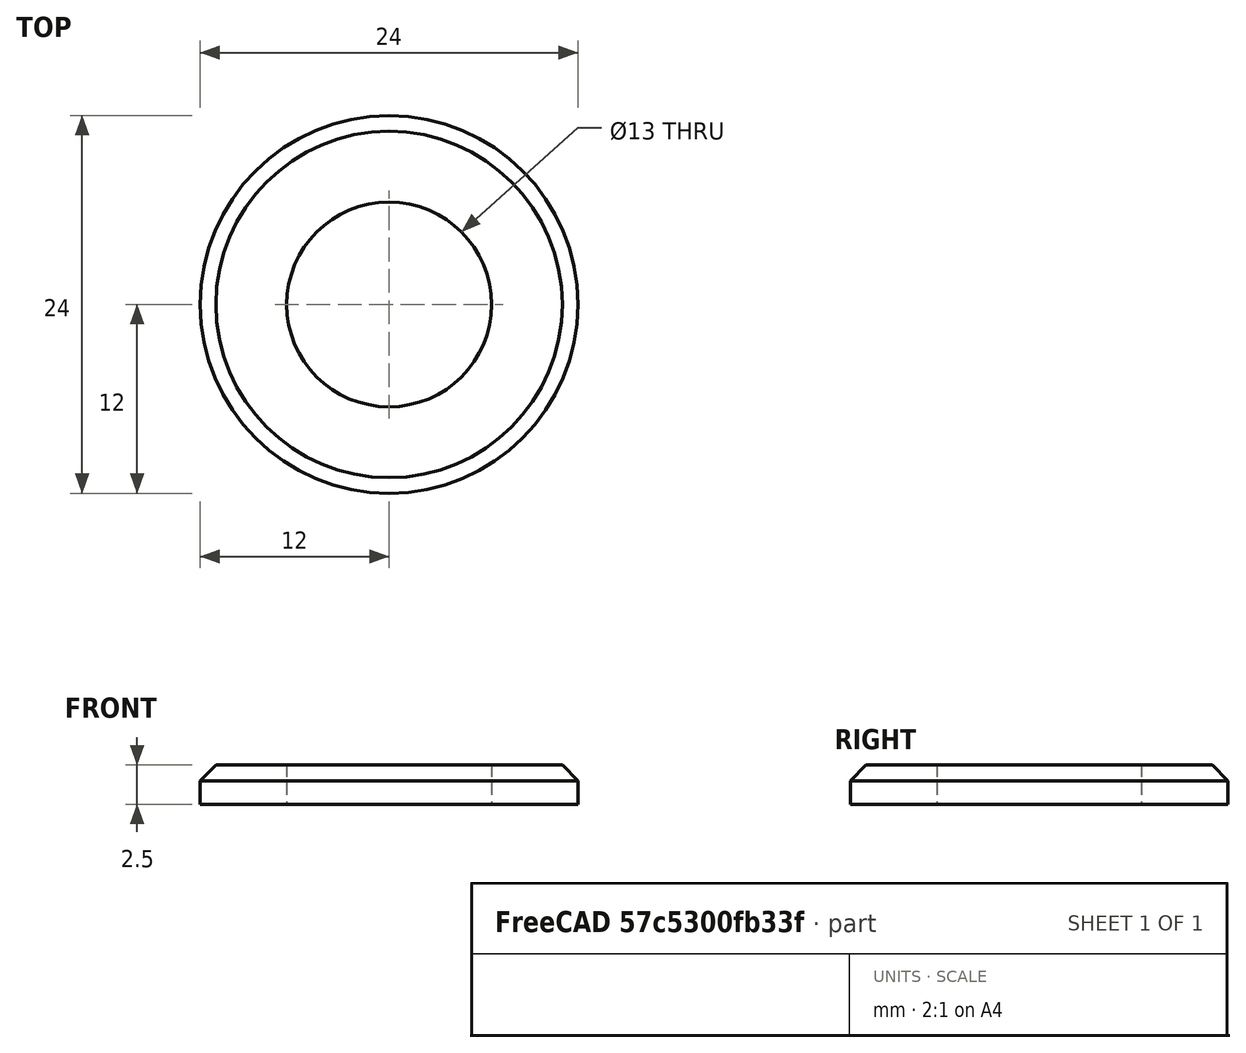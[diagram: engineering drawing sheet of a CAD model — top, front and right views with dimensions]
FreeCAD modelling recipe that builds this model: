
FCSTD DOCUMENT  (FreeCAD 0.15R4651 (Git))
Label: Scheibe_DIN125-B 13
License: CC-BY 3.0
LicenseURL: http://creativecommons.org/licenses/by/3.0/
objects: Sketcher::SketchObject×1, PartDesign::Revolution×1
note: 3 computed .brp shape members not serialized (recipe doc carries the construction recipe); baked Part::Feature solids carry a one-line shape summary decoded from their .brp

FEATURE [Sketcher::SketchObject] Sketch
  Placement = pos=(0,0,0) rot=(0.57735,0.57735,0.57735;2.0944rad)
  sketch-geometry (5):
    g0: LineSegment StartX=6.5 StartY=0 StartZ=0 EndX=12 EndY=0 EndZ=0
    g1: LineSegment StartX=12 StartY=0 StartZ=0 EndX=12 EndY=1.5 EndZ=0
    g2: LineSegment StartX=11 StartY=2.5 StartZ=0 EndX=6.5 EndY=2.5 EndZ=0
    g3: LineSegment StartX=6.5 StartY=2.5 StartZ=0 EndX=6.5 EndY=0 EndZ=0
    g4: LineSegment StartX=11 StartY=2.5 StartZ=0 EndX=12 EndY=1.5 EndZ=0
  constraints (15):
    c: Coincident(g0,g1)
    c: Coincident(g2,g3)
    c: Coincident(g3,g0)
    c: Horizontal(g0)
    c: Horizontal(g2)
    c: Vertical(g1)
    c: Vertical(g3)
    c: PointOnObject(g0,g-1)
    c: DistanceX(g-1,g2) = 6.5
    c: Coincident(g1,g4)
    c: Coincident(g2,g4)
    c: DistanceY(g3) = -2.5
    c: DistanceX(g-1,g1) = 12
    c: DistanceX(g4) = 1
    c: DistanceY(g4) = -1
FEATURE [PartDesign::Revolution] Revolution  label="Scheibe DIN 125 - B 13 #"
  Angle = 360
  Axis = (0,0,1)
  Base = (0,0,0)
  Placement = pos=(0,0,0) rot=(0.57735,0.57735,0.57735;2.0944rad)
  ReferenceAxis = -> Sketch [V_Axis]
  Reversed = true
  Sketch = -> Sketch
